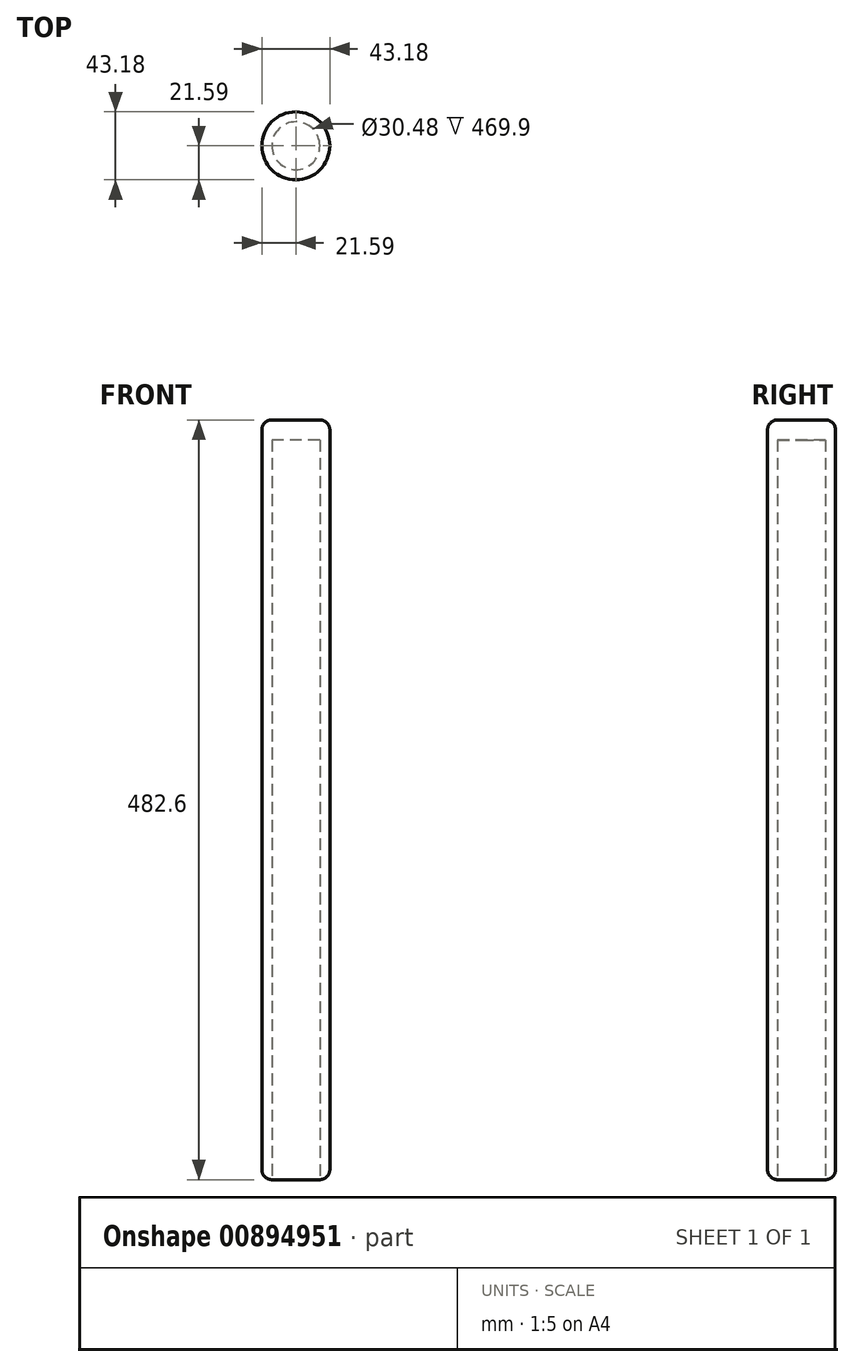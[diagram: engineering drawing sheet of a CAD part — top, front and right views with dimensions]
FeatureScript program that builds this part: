
annotation { "Feature Type Name" : "Feature", "Feature Type Description" : "" }
export const myFeature = defineFeature(function(context is Context, id is Id, definition is map)
    precondition{}
    {
        {
            var Q0;
            Q0=qCreatedBy(makeId("Top.planeOp"),FACE);
            var sketch = newSketch(context, id + "F0", { "sketchPlane" : qUnion([Q0])});
            skCircle(sketch, "E0", {"center": v(0, 0) * mm, "radius": 21.6 * mm});
            skSolve(sketch);
        }
        {
            var Q0;
            Q0=makeQuery(id+"F0.imprint","IMPRINT",FACE,{"disambiguationData":[TD([[makeQuery(id+"F0.imprint","IMPRINT",EDGE,{"derivedFrom":sQuery(id+"F0.wireOp",EDGE,"E0")}),1.0]])]});
            extrude(context, id + "F1", {"entities" : qUnion([Q0]), "depth" : 482.6 * mm, "offsetDistance" : 25.4 * mm});
        }
        {
            var Q0;
            Q0=makeQuery(id+"F1.opExtrude","CAP_EDGE",EDGE,{"disambiguationData":[OSD([sQuery(id+"F0.wireOp",EDGE,"E0")])],"isStart":true});
            fillet(context, id + "F2", {"entities" : qUnion([Q0]), "radius" : 6.35 * mm, "tangentPropagation" : true, "allowEdgeOverflow" : false});
        }
        {
            var Q0;
            Q0=makeQuery(id+"F1.opExtrude","CAP_EDGE",EDGE,{"disambiguationData":[OSD([sQuery(id+"F0.wireOp",EDGE,"E0")])],"isStart":false});
            fillet(context, id + "F3", {"entities" : qUnion([Q0]), "radius" : 6.35 * mm, "tangentPropagation" : true, "allowEdgeOverflow" : false});
        }
        {
            var Q0;
            Q0=makeQuery(id+"F1.opExtrude","CAP_FACE",FACE,{"disambiguationData":[OSD([sQuery(id+"F0.wireOp",EDGE,"E0")])],"isStart":true});
            extrude(context, id + "F4", {"entities" : qUnion([Q0]), "operationType" : NewBodyOperationType.REMOVE, "oppositeDirection" : true, "depth" : 469.9 * mm, "offsetDistance" : 25.4 * mm});
        }
    });
